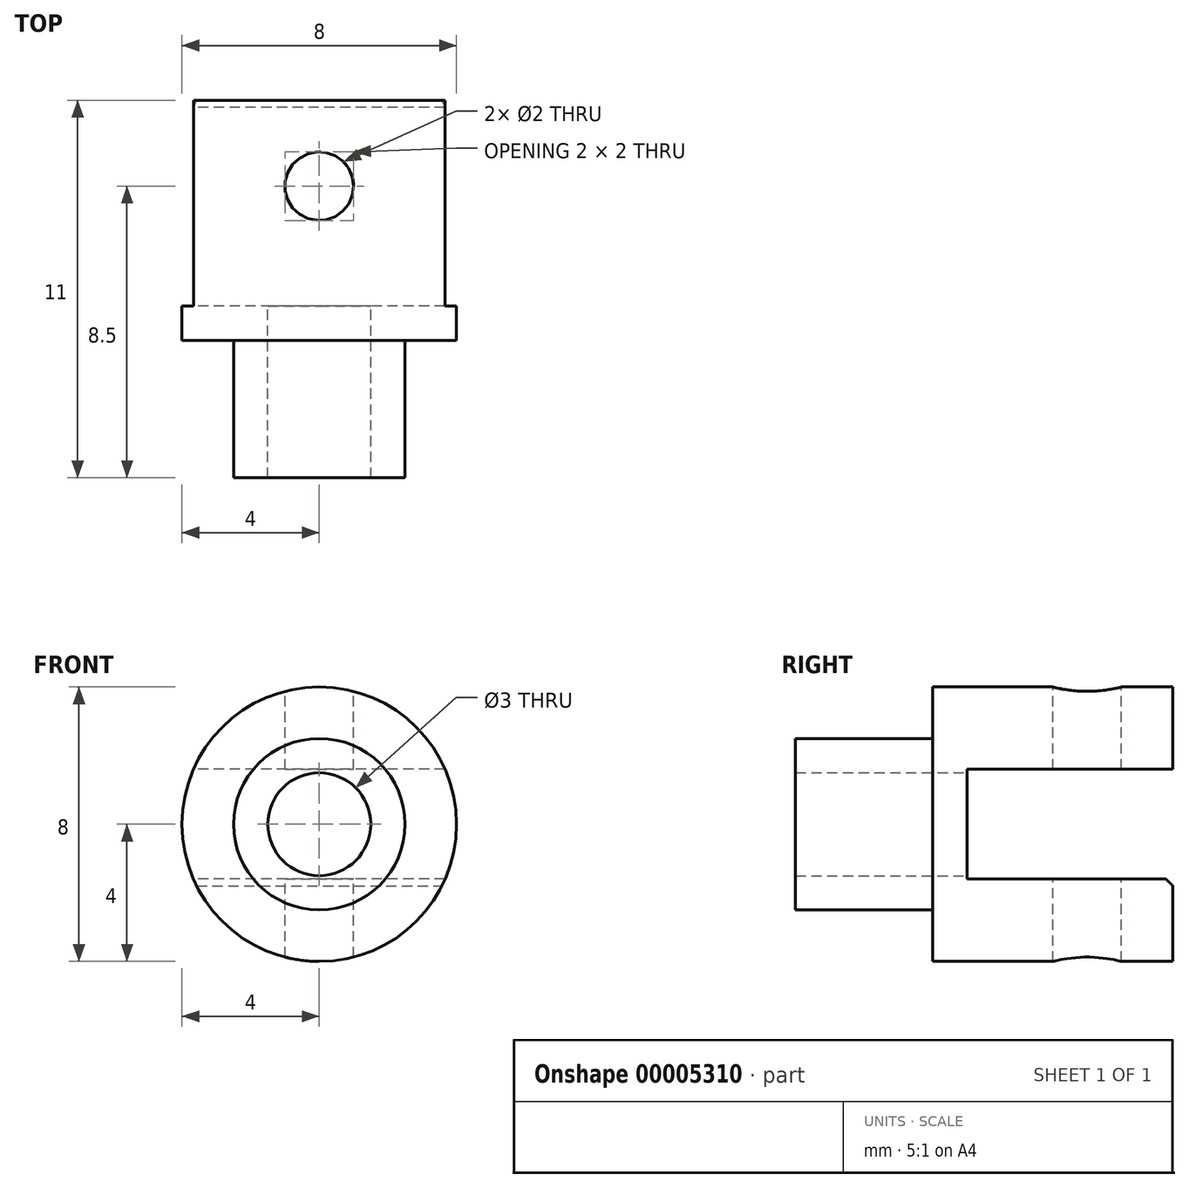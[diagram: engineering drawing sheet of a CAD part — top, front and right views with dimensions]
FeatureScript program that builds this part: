
annotation { "Feature Type Name" : "Feature", "Feature Type Description" : "" }
export const myFeature = defineFeature(function(context is Context, id is Id, definition is map)
    precondition{}
    {
        {
            var Q0;
            Q0=qCreatedBy(makeId("Front.planeOp"),FACE);
            var sketch = newSketch(context, id + "F0", { "sketchPlane" : qUnion([Q0])});
            skCircle(sketch, "E0", {"center": v(0, 0) * mm, "radius": 1.5 * mm});
            skCircle(sketch, "E1", {"center": v(0, 0) * mm, "radius": 2.5 * mm});
            skCircle(sketch, "E2", {"center": v(0, 0) * mm, "radius": 4 * mm});
            skSolve(sketch);
        }
        {
            var Q0;
            Q0=makeQuery(id+"F0.imprint","IMPRINT",FACE,{"disambiguationData":[TD([[makeQuery(id+"F0.imprint","IMPRINT",EDGE,{"derivedFrom":sQuery(id+"F0.wireOp",EDGE,"E0")}),-1.0]])]});
            extrude(context, id + "F1", {"entities" : qUnion([Q0]), "depth" : 4 * mm});
        }
        {
            var Q0;
            Q0=makeQuery(id+"F0.imprint","IMPRINT",FACE,{"disambiguationData":[TD([[makeQuery(id+"F0.imprint","IMPRINT",EDGE,{"derivedFrom":sQuery(id+"F0.wireOp",EDGE,"E1")}),-1.0]])]});
            var Q1;
            Q1=makeQuery(id+"F0.imprint","IMPRINT",FACE,{"disambiguationData":[TD([[makeQuery(id+"F0.imprint","IMPRINT",EDGE,{"derivedFrom":sQuery(id+"F0.wireOp",EDGE,"E0")}),-1.0]])]});
            extrude(context, id + "F2", {"entities" : qUnion([Q0, Q1]), "operationType" : NewBodyOperationType.ADD, "oppositeDirection" : true, "depth" : 7 * mm});
        }
        {
            var Q0;
            Q0=qCreatedBy(makeId("Top.planeOp"),FACE);
            var sketch = newSketch(context, id + "F3", { "sketchPlane" : qUnion([Q0])});
            skCircle(sketch, "E3", {"center": v(0, 4.5) * mm, "radius": 1 * mm});
            skSolve(sketch);
        }
        {
            var Q0;
            Q0=makeQuery(id+"F3.imprint","IMPRINT",FACE,{"disambiguationData":[TD([[makeQuery(id+"F3.imprint","IMPRINT",EDGE,{"derivedFrom":sQuery(id+"F3.wireOp",EDGE,"E3")}),1.0]])]});
            var Q1;
            Q1=sQuery(id+"F3.wireOp",EDGE,"E3");
            extrude(context, id + "F4", {"entities" : qUnion([Q0]), "operationType" : NewBodyOperationType.REMOVE, "surfaceEntities" : qUnion([Q1]), "endBound" : BoundingType.SYMMETRIC, "oppositeDirection" : true, "depth" : 18.5 * mm});
        }
        {
            var Q0;
            Q0=makeQuery(id+"F2.opExtrude","CAP_FACE",FACE,{"disambiguationData":[OSD([sQuery(id+"F0.wireOp",EDGE,"E0"),sQuery(id+"F0.wireOp",EDGE,"E2")])],"isStart":false});
            var sketch = newSketch(context, id + "F5", { "sketchPlane" : qUnion([Q0])});
            skLineSegment(sketch, "E4.bottom", {"start": v(-6.01, 1.6) * mm, "end": v(6, 1.6) * mm});
            skLineSegment(sketch, "E4.top", {"start": v(-6.01, -1.6) * mm, "end": v(6, -1.6) * mm});
            skLineSegment(sketch, "E4.left", {"start": v(-6.01, 1.6) * mm, "end": v(-6.01, -1.6) * mm});
            skLineSegment(sketch, "E4.right", {"start": v(6, 1.6) * mm, "end": v(6, -1.6) * mm});
            skSolve(sketch);
        }
        {
            var Q0;
            Q0=makeQuery(id+"F5.imprint","IMPRINT",FACE,{"disambiguationData":[TD([[makeQuery(id+"F5.imprint","IMPRINT",EDGE,{"derivedFrom":makeQuery(id+"F2.opExtrude","CAP_EDGE",EDGE,{"disambiguationData":[OSD([sQuery(id+"F0.wireOp",EDGE,"E0")])],"isStart":false})}),1.0]])]});
            extrude(context, id + "F6", {"entities" : qUnion([Q0]), "operationType" : NewBodyOperationType.REMOVE, "oppositeDirection" : true, "depth" : 6 * mm});
        }
        {
            var Q0;
            Q0=makeQuery(id+"F6.boolean.opBoolean","COPY",EDGE,{"derivedFrom":makeQuery(id+"F6.opExtrude","CAP_EDGE",EDGE,{"disambiguationData":[OSD([sQuery(id+"F5.wireOp",EDGE,"E4.top")])],"isStart":true})});
            var Q1;
            Q1=makeQuery(id+"F6.boolean.opBoolean","COPY",EDGE,{"derivedFrom":makeQuery(id+"F6.opExtrude","CAP_EDGE",EDGE,{"disambiguationData":[OSD([sQuery(id+"F5.wireOp",EDGE,"E4.bottom")])],"isStart":true})});
            chamfer(context, id + "F7", {"entities" : qUnion([Q0, Q1]), "width" : 0.2 * mm, "tangentPropagation" : true});
        }
    });
